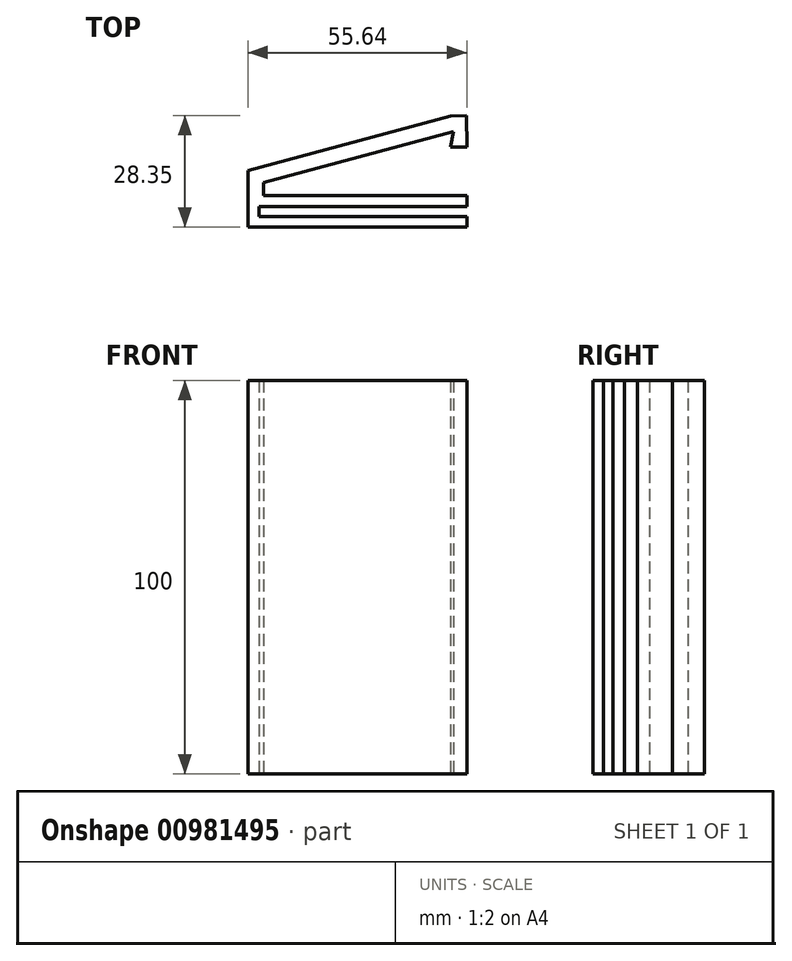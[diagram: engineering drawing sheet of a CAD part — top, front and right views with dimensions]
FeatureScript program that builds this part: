
annotation { "Feature Type Name" : "Feature", "Feature Type Description" : "" }
export const myFeature = defineFeature(function(context is Context, id is Id, definition is map)
    precondition{}
    {
        {
            var Q0;
            Q0=qCreatedBy(makeId("Front.planeOp"),FACE);
            var sketch = newSketch(context, id + "F0", { "sketchPlane" : qUnion([Q0])});
            skLineSegment(sketch, "E0.bottom", {"start": v(-27.82, 50) * mm, "end": v(27.82, 50) * mm});
            skLineSegment(sketch, "E0.top", {"start": v(-27.82, -50) * mm, "end": v(27.82, -50) * mm});
            skLineSegment(sketch, "E0.left", {"start": v(-27.82, 50) * mm, "end": v(-27.82, -50) * mm});
            skLineSegment(sketch, "E0.right", {"start": v(27.82, 50) * mm, "end": v(27.82, -50) * mm});
            skLineSegment(sketch, "E1", {"start": v(27.82, 40) * mm, "end": v(-78.3, 40) * mm, "construction": true});
            skPoint(sketch, "E2", {"position": v(-27.82, 0) * mm});
            skLineSegment(sketch, "E3", {"start": v(-61.14, 0) * mm, "end": v(109.13, 0) * mm, "construction": true});
            skLineSegment(sketch, "E4", {"start": v(0, -83.7) * mm, "end": v(0, 95.89) * mm, "construction": true});
            skPoint(sketch, "E4.startSnap0", {"position": v(0, -50) * mm});
            skPoint(sketch, "E5", {"position": v(0, 0) * mm});
            skSolve(sketch);
        }
        {
            var Q0;
            Q0=makeQuery(id+"F0.imprint","IMPRINT",FACE,{"disambiguationData":[TD([[makeQuery(id+"F0.imprint","IMPRINT",EDGE,{"derivedFrom":sQuery(id+"F0.wireOp",EDGE,"E0.bottom")}),-1.0]])]});
            extrude(context, id + "F1", {"entities" : qUnion([Q0]), "oppositeDirection" : true, "depth" : 8 * mm, "offsetDistance" : 25 * mm});
        }
        {
            var Q0;
            Q0=qCreatedBy(makeId("Right.planeOp"),FACE);
            var sketch = newSketch(context, id + "F2", { "sketchPlane" : qUnion([Q0])});
            skLineSegment(sketch, "E6", {"start": v(3.8, 51.3) * mm, "end": v(3.8, -48.28) * mm, "construction": true});
            skLineSegment(sketch, "E7.bottom", {"start": v(2.68, 86.75) * mm, "end": v(5.18, 86.75) * mm});
            skLineSegment(sketch, "E7.top", {"start": v(2.68, -71.33) * mm, "end": v(5.18, -71.33) * mm});
            skLineSegment(sketch, "E7.left", {"start": v(2.68, 86.75) * mm, "end": v(2.68, -71.33) * mm});
            skLineSegment(sketch, "E7.right", {"start": v(5.18, 86.75) * mm, "end": v(5.18, -71.33) * mm});
            skSolve(sketch);
        }
        {
            var Q0;
            Q0=makeQuery(id+"FBMLdxI11pTwmpj_1.opExtractSurface","COPY",FACE,{"derivedFrom":makeQuery(id+"F2.imprint","IMPRINT",FACE,{"disambiguationData":[TD([[makeQuery(id+"F2.imprint","IMPRINT",EDGE,{"derivedFrom":sQuery(id+"F2.wireOp",EDGE,"E7.bottom")}),-1.0]])]})});
            var Q1;
            Q1=makeQuery(id+"F2.imprint","IMPRINT",FACE,{"disambiguationData":[TD([[makeQuery(id+"F2.imprint","IMPRINT",EDGE,{"derivedFrom":sQuery(id+"F2.wireOp",EDGE,"E7.bottom")}),-1.0]])]});
            extrude(context, id + "F3", {"entities" : qUnion([Q0, Q1]), "operationType" : NewBodyOperationType.REMOVE, "endBound" : BoundingType.THROUGH_ALL, "depth" : 25 * mm, "offsetDistance" : 25 * mm, "hasSecondDirection" : true, "secondDirectionOppositeDirection" : true, "secondDirectionDepth" : 25 * mm});
        }
        {
            var Q0;
            Q0=qCreatedBy(makeId("Top.planeOp"),FACE);
            var sketch = newSketch(context, id + "F4", { "sketchPlane" : qUnion([Q0])});
            skLineSegment(sketch, "E8", {"start": v(-27.82, 14.37) * mm, "end": v(23.67, 28.17) * mm});
            skLineSegment(sketch, "E9", {"start": v(23.67, 28.17) * mm, "end": v(27.67, 28.35) * mm});
            skLineSegment(sketch, "E10", {"start": v(27.67, 28.35) * mm, "end": v(27.82, 20.27) * mm});
            skLineSegment(sketch, "E11", {"start": v(27.82, 20.27) * mm, "end": v(23.67, 20.27) * mm});
            skLineSegment(sketch, "E12", {"start": v(23.67, 20.27) * mm, "end": v(24.37, 24.22) * mm});
            skLineSegment(sketch, "E13", {"start": v(24.37, 24.22) * mm, "end": v(-23.82, 11.3) * mm});
            skLineSegment(sketch, "E14", {"start": v(-23.82, 11.3) * mm, "end": v(-23.82, 8) * mm});
            skLineSegment(sketch, "E15.0", {"start": v(-27.82, 8) * mm, "end": v(-27.82, 0) * mm, "construction": true});
            skLineSegment(sketch, "E16.0", {"start": v(-27.82, 8) * mm, "end": v(27.82, 8) * mm, "construction": true});
            skLineSegment(sketch, "E17", {"start": v(-27.82, 8) * mm, "end": v(-27.82, 14.37) * mm});
            skLineSegment(sketch, "E18", {"start": v(-23.82, 8) * mm, "end": v(-27.82, 8) * mm});
            skSolve(sketch);
        }
        {
            var Q0;
            Q0 = qSketchRegion(id + "F4", true);
            extrude(context, id + "F5", {"entities" : qUnion([Q0]), "operationType" : NewBodyOperationType.ADD, "endBound" : BoundingType.SYMMETRIC, "depth" : 100 * mm, "offsetDistance" : 25 * mm});
        }
    });
